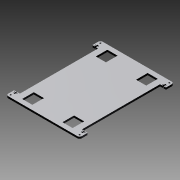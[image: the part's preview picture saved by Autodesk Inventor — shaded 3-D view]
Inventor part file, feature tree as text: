
AUTODESK INVENTOR PART (.ipt)
format: ipt  version: 2013 (Build 170138000, 138)  size: 244,224 bytes
history: native  units: mm
features: extrude x2, mirror x2, sketch x2, fillet x1, reference x1
ambient origin geometry x8: Origin, YZ Plane, XZ Plane, XY Plane, X Axis, Y Axis, Z Axis, Center Point
bodies: Solid1 (feature_tree)
feature tree (8):
  extrude  "Extrusion1"  Depth=4.0mm
  fillet  "Fillet1"  Radius=10.0mm
  mirror  "Mirror1"
  mirror  "Mirror2"
  extrude  "Extrusion2"  Depth=10.0mm
  sketch  "Sketch1"  dims[d1=145.0mm d3=4.0mm d4=10.0mm]
  sketch  "Sketch2"  dims[d5=10.0mm d6=10.0mm d7=127.0mm d8=8.0mm d9=10.0mm d10=5.0mm d11=6.477mm d12=0.0mm d13=2.0mm d14=4.0mm d15=8.0mm d16=1.5mm d17=4.0mm d18=40.0mm d19=35.0mm d20=127.0mm d21=20.0mm d22=12.5mm d24=12.5mm d25=10.0mm d26=0.0mm]
  reference  "Reference1"
